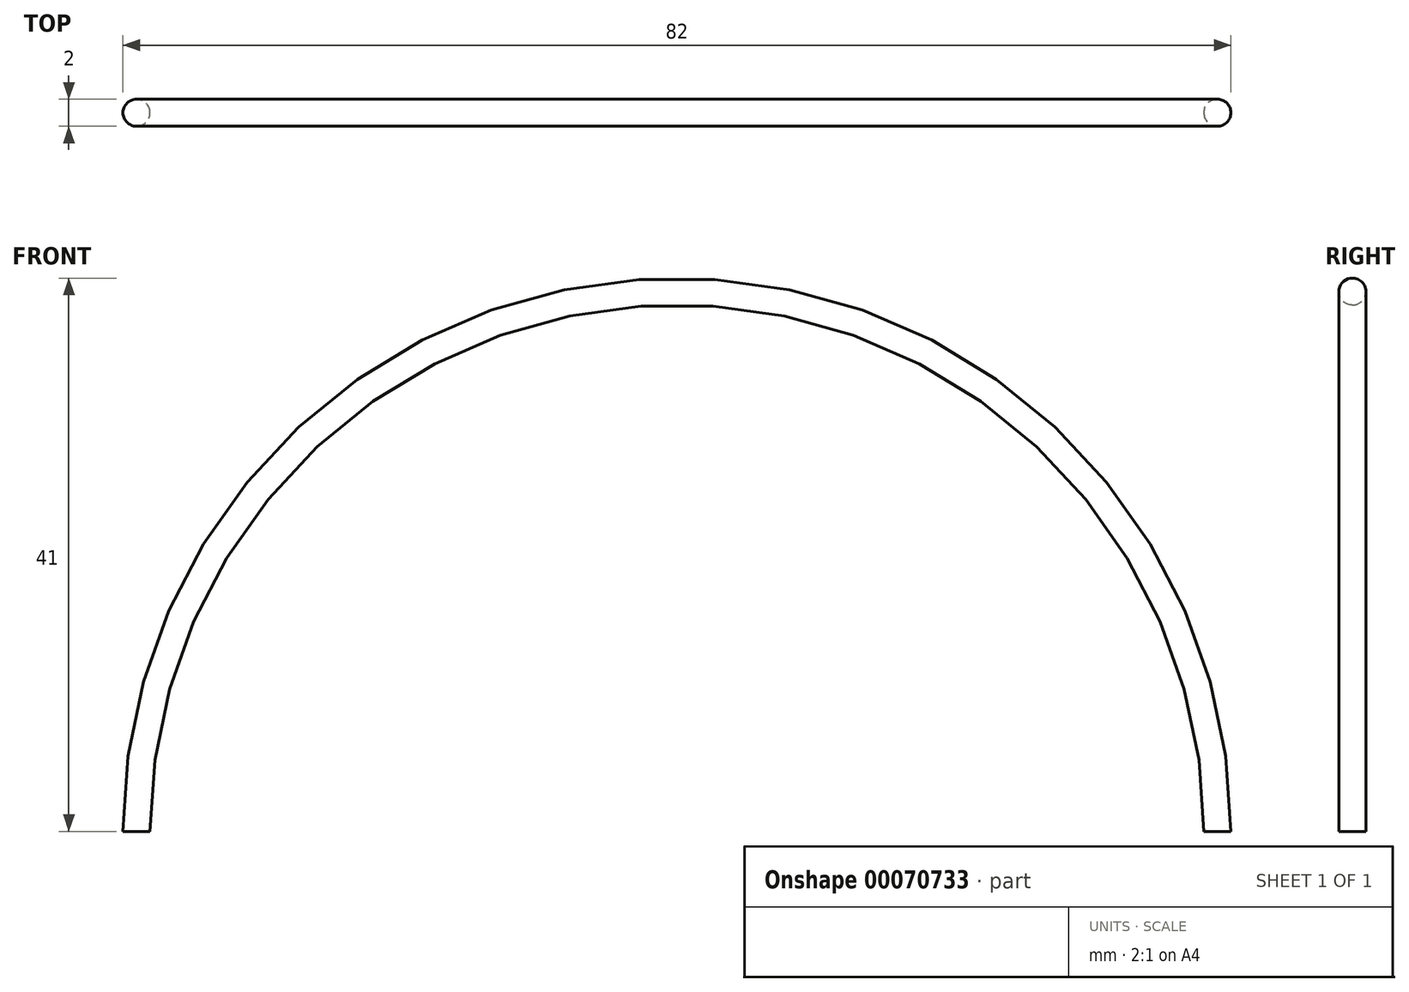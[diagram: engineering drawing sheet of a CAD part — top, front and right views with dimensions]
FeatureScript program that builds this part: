
annotation { "Feature Type Name" : "Feature", "Feature Type Description" : "" }
export const myFeature = defineFeature(function(context is Context, id is Id, definition is map)
    precondition{}
    {
        {
            var Q0;
            Q0=qCreatedBy(makeId("Front.planeOp"),FACE);
            var sketch = newSketch(context, id + "F0", { "sketchPlane" : qUnion([Q0])});
            skArc(sketch, "E0", {"start": v(-40, 0) * mm, "mid": v(0, 40) * mm, "end": v(40, 0) * mm});
            skSolve(sketch);
        }
        {
            var Q0;
            Q0=qCreatedBy(makeId("Top.planeOp"),FACE);
            var sketch = newSketch(context, id + "F1", { "sketchPlane" : qUnion([Q0])});
            skCircle(sketch, "E1", {"center": v(-40, 0) * mm, "radius": 1 * mm});
            skSolve(sketch);
        }
        {
            var Q0;
            Q0=makeQuery(id+"F1.imprint","IMPRINT",FACE,{"disambiguationData":[TD([[makeQuery(id+"F1.imprint","IMPRINT",EDGE,{"derivedFrom":sQuery(id+"F1.wireOp",EDGE,"E1")}),1.0]])]});
            var Q1;
            Q1=sQuery(id+"F0.wireOp",EDGE,"E0");
            sweep(context, id + "F2", {"profiles" : qUnion([Q0]), "path" : qUnion([Q1])});
        }
    });
